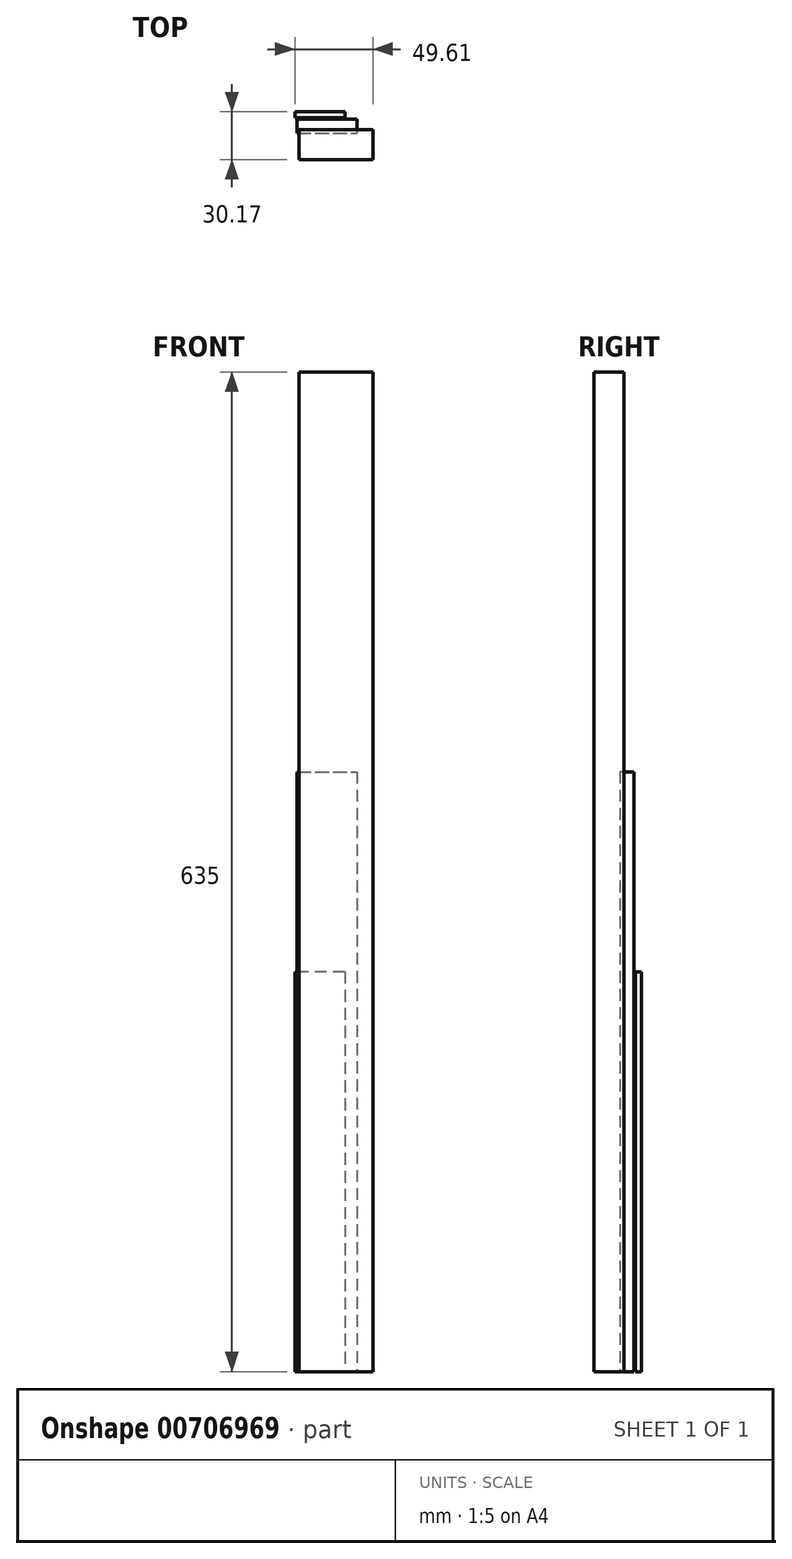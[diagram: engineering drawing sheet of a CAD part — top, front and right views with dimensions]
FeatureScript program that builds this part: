
annotation { "Feature Type Name" : "Feature", "Feature Type Description" : "" }
export const myFeature = defineFeature(function(context is Context, id is Id, definition is map)
    precondition{}
    {
        {
            var Q0;
            Q0=qCreatedBy(makeId("Top.planeOp"),FACE);
            var sketch = newSketch(context, id + "F0", { "sketchPlane" : qUnion([Q0])});
            skLineSegment(sketch, "E0.bottom", {"start": v(-25.08, 45.37) * mm, "end": v(-56.83, 45.37) * mm});
            skLineSegment(sketch, "E0.top", {"start": v(-25.08, 41.56) * mm, "end": v(-56.83, 41.56) * mm});
            skLineSegment(sketch, "E0.left", {"start": v(-25.08, 45.37) * mm, "end": v(-25.08, 41.56) * mm});
            skLineSegment(sketch, "E0.right", {"start": v(-56.83, 45.37) * mm, "end": v(-56.83, 41.56) * mm});
            skSolve(sketch);
        }
        {
            var Q0;
            Q0=qCreatedBy(makeId("Top.planeOp"),FACE);
            var sketch = newSketch(context, id + "F1", { "sketchPlane" : qUnion([Q0])});
            skLineSegment(sketch, "E1.bottom", {"start": v(-55.5, 40.65) * mm, "end": v(-17.4, 40.65) * mm});
            skLineSegment(sketch, "E1.top", {"start": v(-55.5, 31.76) * mm, "end": v(-17.4, 31.76) * mm});
            skLineSegment(sketch, "E1.left", {"start": v(-55.5, 40.65) * mm, "end": v(-55.5, 31.76) * mm});
            skLineSegment(sketch, "E1.right", {"start": v(-17.4, 40.65) * mm, "end": v(-17.4, 31.76) * mm});
            skSolve(sketch);
        }
        {
            var Q0;
            Q0=qCreatedBy(makeId("Top.planeOp"),FACE);
            var sketch = newSketch(context, id + "F2", { "sketchPlane" : qUnion([Q0])});
            skLineSegment(sketch, "E2.bottom", {"start": v(-54.2, 34.25) * mm, "end": v(-7.22, 34.25) * mm});
            skLineSegment(sketch, "E2.top", {"start": v(-54.2, 15.2) * mm, "end": v(-7.22, 15.2) * mm});
            skLineSegment(sketch, "E2.left", {"start": v(-54.2, 34.25) * mm, "end": v(-54.2, 15.2) * mm});
            skLineSegment(sketch, "E2.right", {"start": v(-7.22, 34.25) * mm, "end": v(-7.22, 15.2) * mm});
            skSolve(sketch);
        }
        {
            var Q0;
            Q0 = qSketchRegion(id + "F0", true);
            extrude(context, id + "F3", {"entities" : qUnion([Q0]), "depth" : 254 * mm, "offsetDistance" : 25.4 * mm});
        }
        {
            var Q0;
            Q0 = qSketchRegion(id + "F1", true);
            extrude(context, id + "F4", {"entities" : qUnion([Q0]), "depth" : 381 * mm, "offsetDistance" : 25.4 * mm});
        }
        {
            var Q0;
            Q0 = qSketchRegion(id + "F2", true);
            extrude(context, id + "F5", {"entities" : qUnion([Q0]), "depth" : 635 * mm, "offsetDistance" : 25.4 * mm});
        }
    });
